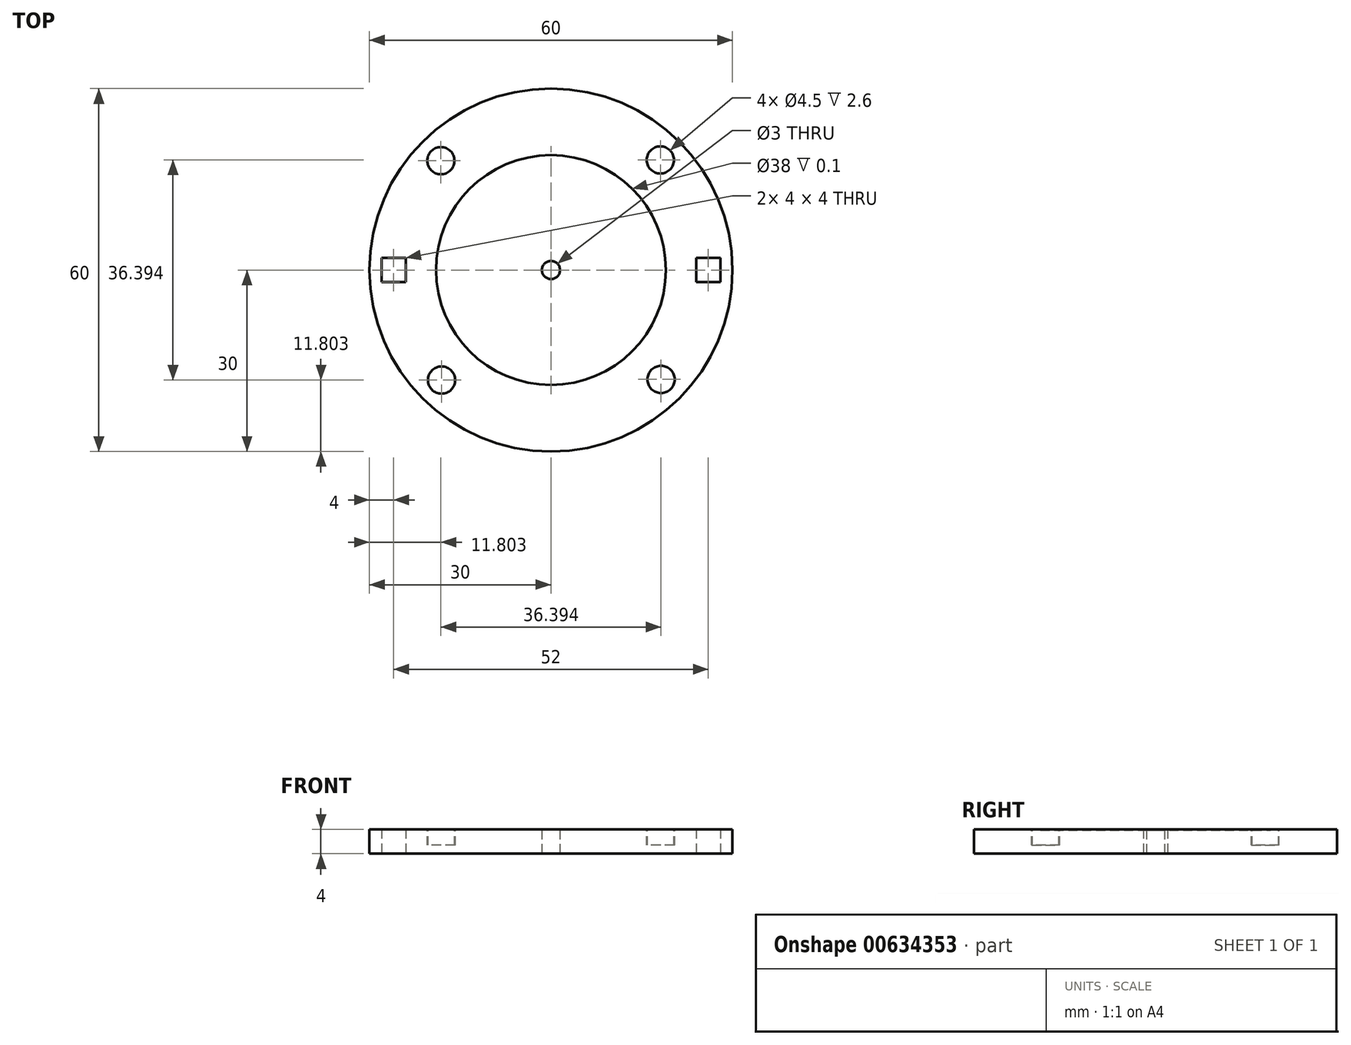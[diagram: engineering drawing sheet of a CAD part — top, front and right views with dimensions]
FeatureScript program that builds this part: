
annotation { "Feature Type Name" : "Feature", "Feature Type Description" : "" }
export const myFeature = defineFeature(function(context is Context, id is Id, definition is map)
    precondition{}
    {
        {
            var Q0;
            Q0=qCreatedBy(makeId("Top.planeOp"),FACE);
            var sketch = newSketch(context, id + "F0", { "sketchPlane" : qUnion([Q0])});
            skCircle(sketch, "E0", {"center": v(0, 0) * mm, "radius": 30 * mm});
            skLineSegment(sketch, "E1", {"start": v(-30, 0) * mm, "end": v(30, 0) * mm, "construction": true});
            skCircle(sketch, "E2", {"center": v(0, 0) * mm, "radius": 19 * mm, "construction": true});
            skLineSegment(sketch, "E3.bottom", {"start": v(-28, 2) * mm, "end": v(-24, 2) * mm});
            skLineSegment(sketch, "E3.top", {"start": v(-28, -2) * mm, "end": v(-24, -2) * mm});
            skLineSegment(sketch, "E3.left", {"start": v(-28, 2) * mm, "end": v(-28, -2) * mm});
            skLineSegment(sketch, "E3.right", {"start": v(-24, 2) * mm, "end": v(-24, -2) * mm});
            skLineSegment(sketch, "E4.bottom", {"start": v(24, 2) * mm, "end": v(28, 2) * mm});
            skLineSegment(sketch, "E4.top", {"start": v(24, -2) * mm, "end": v(28, -2) * mm});
            skLineSegment(sketch, "E4.left", {"start": v(24, 2) * mm, "end": v(24, -2) * mm});
            skLineSegment(sketch, "E4.right", {"start": v(28, 2) * mm, "end": v(28, -2) * mm});
            skCircle(sketch, "E5", {"center": v(0, 0) * mm, "radius": 1.5 * mm});
            skSolve(sketch);
        }
        {
            var Q0;
            Q0=makeQuery(id+"F0.imprint","IMPRINT",FACE,{"disambiguationData":[TD([[makeQuery(id+"F0.imprint","IMPRINT",EDGE,{"derivedFrom":sQuery(id+"F0.wireOp",EDGE,"E0")}),1.0]])]});
            extrude(context, id + "F1", {"entities" : qUnion([Q0]), "depth" : 4 * mm, "offsetDistance" : 25 * mm});
        }
        {
            var Q0;
            Q0=makeQuery(id+"F1.opExtrude","CAP_FACE",FACE,{"disambiguationData":[OSD([sQuery(id+"F0.wireOp",EDGE,"E0"),sQuery(id+"F0.wireOp",EDGE,"E3.bottom"),sQuery(id+"F0.wireOp",EDGE,"E3.top"),sQuery(id+"F0.wireOp",EDGE,"E3.left"),sQuery(id+"F0.wireOp",EDGE,"E3.right"),sQuery(id+"F0.wireOp",EDGE,"E4.bottom"),sQuery(id+"F0.wireOp",EDGE,"E4.top"),sQuery(id+"F0.wireOp",EDGE,"E4.left"),sQuery(id+"F0.wireOp",EDGE,"E4.right"),sQuery(id+"F0.wireOp",EDGE,"E5")])],"isStart":false});
            var sketch = newSketch(context, id + "F2", { "sketchPlane" : qUnion([Q0])});
            skCircle(sketch, "E6", {"center": v(0, 0) * mm, "radius": 19 * mm});
            skPoint(sketch, "E7", {"position": v(-30, 0) * mm});
            skPoint(sketch, "E8", {"position": v(30, 0) * mm});
            skPoint(sketch, "E9", {"position": v(0, 30) * mm});
            skPoint(sketch, "E10", {"position": v(0, -30) * mm});
            skLineSegment(sketch, "E11.bottom", {"start": v(30.1, -30) * mm, "end": v(-30.1, -30) * mm, "construction": true});
            skLineSegment(sketch, "E11.top", {"start": v(30.1, 30) * mm, "end": v(-30.1, 30) * mm, "construction": true});
            skLineSegment(sketch, "E11.left", {"start": v(30.1, -30) * mm, "end": v(30.1, 30) * mm, "construction": true});
            skLineSegment(sketch, "E11.right", {"start": v(-30.1, -30) * mm, "end": v(-30.1, 30) * mm, "construction": true});
            skLineSegment(sketch, "E12", {"start": v(0, 0) * mm, "end": v(-30.1, 30) * mm, "construction": true});
            skLineSegment(sketch, "E13", {"start": v(0, 0) * mm, "end": v(30.1, -30) * mm, "construction": true});
            skLineSegment(sketch, "E14", {"start": v(0, 0) * mm, "end": v(-30.1, -30) * mm, "construction": true});
            skLineSegment(sketch, "E15", {"start": v(0, 0) * mm, "end": v(30.1, 30) * mm, "construction": true});
            skCircle(sketch, "E16", {"center": v(-18.2, 18.08) * mm, "radius": 2.25 * mm});
            skCircle(sketch, "E17.1.0", {"center": v(-18.08, -18.2) * mm, "radius": 2.25 * mm});
            skCircle(sketch, "E17.2.0", {"center": v(18.2, -18.08) * mm, "radius": 2.25 * mm});
            skCircle(sketch, "E17.3.0", {"center": v(18.08, 18.2) * mm, "radius": 2.25 * mm});
            skLineSegment(sketch, "E18", {"start": v(-24, -2) * mm, "end": v(24, -2) * mm});
            skLineSegment(sketch, "E19", {"start": v(-28, -0.76) * mm, "end": v(28, -0.76) * mm});
            skSolve(sketch);
        }
        {
            var Q0;
            Q0=makeQuery(id+"F2.imprint","IMPRINT",FACE,{"disambiguationData":[TD([[makeQuery(id+"F2.imprint","IMPRINT",EDGE,{"derivedFrom":sQuery(id+"F2.wireOp",EDGE,"E16")}),1.0]])]});
            var Q1;
            Q1=makeQuery(id+"F2.imprint","IMPRINT",FACE,{"disambiguationData":[TD([[makeQuery(id+"F2.imprint","IMPRINT",EDGE,{"derivedFrom":sQuery(id+"F2.wireOp",EDGE,"E17.3.0")}),1.0]])]});
            var Q2;
            Q2=makeQuery(id+"F2.imprint","IMPRINT",FACE,{"disambiguationData":[TD([[makeQuery(id+"F2.imprint","IMPRINT",EDGE,{"derivedFrom":sQuery(id+"F2.wireOp",EDGE,"E17.1.0")}),1.0]])]});
            var Q3;
            Q3=makeQuery(id+"F2.imprint","IMPRINT",FACE,{"disambiguationData":[TD([[makeQuery(id+"F2.imprint","IMPRINT",EDGE,{"derivedFrom":sQuery(id+"F2.wireOp",EDGE,"E17.2.0")}),1.0]])]});
            var Q4;
            Q4=sQuery(id+"F2.wireOp",EDGE,"E16");
            var Q5;
            Q5=sQuery(id+"F2.wireOp",EDGE,"E17.1.0");
            var Q6;
            Q6=sQuery(id+"F2.wireOp",EDGE,"E17.2.0");
            var Q7;
            Q7=sQuery(id+"F2.wireOp",EDGE,"E17.3.0");
            extrude(context, id + "F3", {"entities" : qUnion([Q0, Q1, Q2, Q3]), "operationType" : NewBodyOperationType.REMOVE, "surfaceEntities" : qUnion([Q4, Q5, Q6, Q7]), "oppositeDirection" : true, "depth" : 2.6 * mm, "offsetDistance" : 25 * mm});
        }
        {
            var Q0;
            Q0=makeQuery(id+"F1.opExtrude","CAP_FACE",FACE,{"disambiguationData":[OSD([sQuery(id+"F0.wireOp",EDGE,"E0"),sQuery(id+"F0.wireOp",EDGE,"E3.bottom"),sQuery(id+"F0.wireOp",EDGE,"E3.top"),sQuery(id+"F0.wireOp",EDGE,"E3.left"),sQuery(id+"F0.wireOp",EDGE,"E3.right"),sQuery(id+"F0.wireOp",EDGE,"E4.bottom"),sQuery(id+"F0.wireOp",EDGE,"E4.top"),sQuery(id+"F0.wireOp",EDGE,"E4.left"),sQuery(id+"F0.wireOp",EDGE,"E4.right"),sQuery(id+"F0.wireOp",EDGE,"E5")])],"isStart":false});
            var sketch = newSketch(context, id + "F4", { "sketchPlane" : qUnion([Q0])});
            skCircle(sketch, "E20", {"center": v(0, 0) * mm, "radius": 19 * mm});
            skSolve(sketch);
        }
        {
            var Q0;
            Q0=makeQuery(id+"F4.imprint","IMPRINT",FACE,{"disambiguationData":[TD([[makeQuery(id+"F4.imprint","IMPRINT",EDGE,{"derivedFrom":sQuery(id+"F4.wireOp",EDGE,"E20")}),1.0]])]});
            extrude(context, id + "F5", {"entities" : qUnion([Q0]), "operationType" : NewBodyOperationType.REMOVE, "oppositeDirection" : true, "depth" : 0.1 * mm, "offsetDistance" : 25 * mm});
        }
    });
